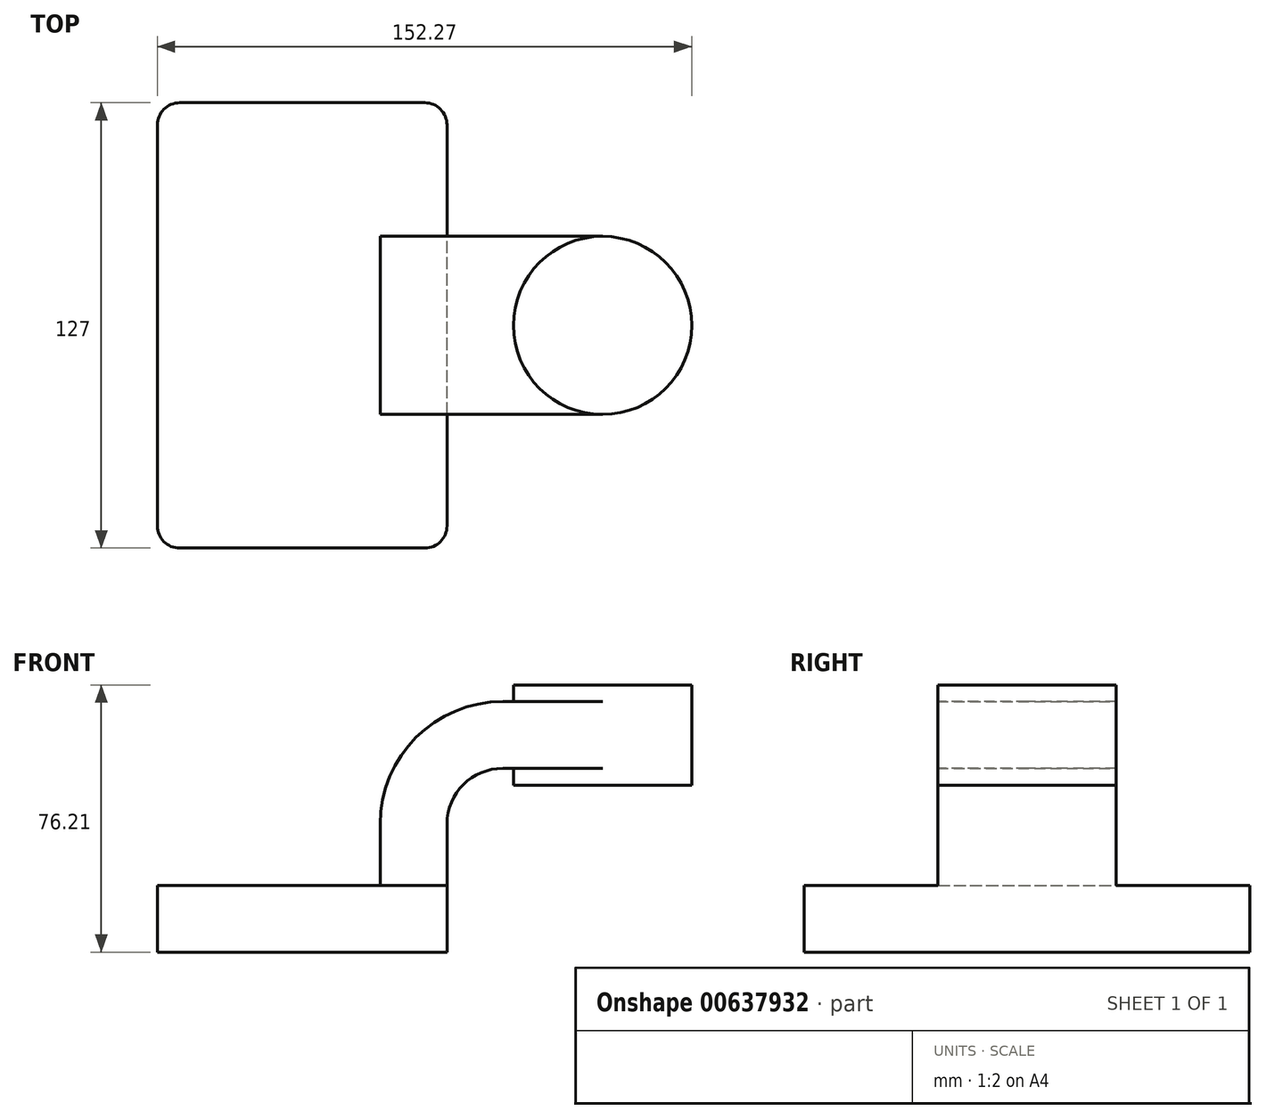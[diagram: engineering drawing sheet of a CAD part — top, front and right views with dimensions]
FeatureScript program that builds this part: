
annotation { "Feature Type Name" : "Feature", "Feature Type Description" : "" }
export const myFeature = defineFeature(function(context is Context, id is Id, definition is map)
    precondition{}
    {
        {
            var Q0;
            Q0=qCreatedBy(makeId("Front.planeOp"),FACE);
            var sketch = newSketch(context, id + "F0", { "sketchPlane" : qUnion([Q0])});
            skLineSegment(sketch, "E0.bottom", {"start": v(-41.28, -9.53) * mm, "end": v(41.28, -9.53) * mm});
            skLineSegment(sketch, "E0.top", {"start": v(-41.28, 9.53) * mm, "end": v(41.28, 9.53) * mm});
            skLineSegment(sketch, "E0.left", {"start": v(-41.28, -9.53) * mm, "end": v(-41.28, 9.53) * mm});
            skLineSegment(sketch, "E0.right", {"start": v(41.28, -9.53) * mm, "end": v(41.28, 9.53) * mm});
            skPoint(sketch, "E0.middle", {"position": v(0, 0) * mm});
            skLineSegment(sketch, "E1", {"start": v(41.28, 9.53) * mm, "end": v(41.28, 27) * mm});
            skArc(sketch, "E2", {"start": v(41.27, 27) * mm, "mid": v(45.92, 38.23) * mm, "end": v(57.15, 42.88) * mm});
            skLineSegment(sketch, "E3.bottom", {"start": v(60.2, 38.1) * mm, "end": v(111, 38.1) * mm});
            skLineSegment(sketch, "E3.top", {"start": v(60.2, 66.67) * mm, "end": v(111, 66.67) * mm});
            skLineSegment(sketch, "E3.left", {"start": v(60.2, 38.1) * mm, "end": v(60.2, 66.67) * mm});
            skLineSegment(sketch, "E3.right", {"start": v(111, 38.1) * mm, "end": v(111, 66.67) * mm});
            skPoint(sketch, "E3.middle", {"position": v(85.6, 52.39) * mm});
            skLineSegment(sketch, "E4", {"start": v(57.15, 42.88) * mm, "end": v(85.72, 42.88) * mm});
            skLineSegment(sketch, "E5.0", {"start": v(57.15, 61.93) * mm, "end": v(85.6, 61.93) * mm});
            skArc(sketch, "E5.1", {"start": v(22.23, 27) * mm, "mid": v(32.45, 51.7) * mm, "end": v(57.15, 61.93) * mm});
            skLineSegment(sketch, "E5.2", {"start": v(22.23, 9.53) * mm, "end": v(22.23, 27) * mm});
            skLineSegment(sketch, "E6", {"start": v(85.6, 38.1) * mm, "end": v(85.6, 66.67) * mm});
            skFitSpline(sketch, "E7", {"points": [v(-41.28, 9.53) * mm, v(57.15, 61.93) * mm], "startDerivative": vector(2.36, 68.58) * mm, "endDerivative": vector(171.45, -0.03) * mm});
            skSolve(sketch);
        }
        {
            var Q0;
            Q0=makeQuery(id+"F0.imprint","IMPRINT",FACE,{"disambiguationData":[TD([[makeQuery(id+"F0.imprint","IMPRINT",EDGE,{"derivedFrom":sQuery(id+"F0.wireOp",EDGE,"E0.bottom")}),1.0]])]});
            extrude(context, id + "F1", {"entities" : qUnion([Q0]), "endBound" : BoundingType.SYMMETRIC, "depth" : 127 * mm, "offsetDistance" : 25.4 * mm});
        }
        {
            var Q0;
            {var subQ5=sQuery(id+"F0.wireOp",EDGE,"E1");Q0=makeQuery(id+"F0.imprint","IMPRINT",FACE,{"disambiguationData":[TD([[makeQuery(id+"F0.imprint","IMPRINT",EDGE,{"derivedFrom":subQ5}),1.0]])]});}
            var Q1;
            {var subQ0=sQuery(id+"F0.wireOp",EDGE,"E4");var subQ1=sQuery(id+"F0.wireOp",EDGE,"E3.left");var subQ2=makeQuery(id+"F0.imprint","INTERSECT",VERTEX,{"derivedFrom":[subQ1,subQ0]});Q1=makeQuery(id+"F0.imprint","IMPRINT",FACE,{"disambiguationData":[TD([[makeQuery(id+"F0.imprint","IMPRINT",EDGE,{"disambiguationData":[TD([[subQ2,-1.0]])],"derivedFrom":subQ1}),-1.0]])]});}
            extrude(context, id + "F2", {"entities" : qUnion([Q0, Q1]), "operationType" : NewBodyOperationType.ADD, "endBound" : BoundingType.SYMMETRIC, "depth" : 50.8 * mm, "offsetDistance" : 25.4 * mm});
        }
        {
            var Q0;
            Q0=makeQuery(id+"F0.imprint","IMPRINT",FACE,{"disambiguationData":[TD([[makeQuery(id+"F0.imprint","IMPRINT",EDGE,{"derivedFrom":sQuery(id+"F0.wireOp",EDGE,"E5.1")}),1.0]])]});
            extrude(context, id + "F3", {"entities" : qUnion([Q0]), "operationType" : NewBodyOperationType.ADD, "endBound" : BoundingType.SYMMETRIC, "depth" : 15.88 * mm, "offsetDistance" : 25.4 * mm});
        }
        {
            var Q0;
            {var subQ4=sQuery(id+"F0.wireOp",EDGE,"E3.right");Q0=makeQuery(id+"F0.imprint","IMPRINT",FACE,{"disambiguationData":[TD([[makeQuery(id+"F0.imprint","IMPRINT",EDGE,{"derivedFrom":subQ4}),1.0]])]});}
            var Q1;
            Q1=sQuery(id+"F0.wireOp",EDGE,"E6");
            revolve(context, id + "F4", {"operationType" : NewBodyOperationType.ADD, "entities" : qUnion([Q0]), "axis" : qUnion([Q1]), "revolveType" : RevolveType.FULL});
        }
        {
            var Q0;
            Q0=makeQuery(id+"F1.opExtrude","CAP_EDGE",EDGE,{"disambiguationData":[OSD([sQuery(id+"F0.wireOp",EDGE,"E0.left")])],"isStart":false});
            var Q1;
            Q1=makeQuery(id+"F1.opExtrude","CAP_EDGE",EDGE,{"disambiguationData":[OSD([sQuery(id+"F0.wireOp",EDGE,"E0.right")])],"isStart":false});
            var Q2;
            Q2=makeQuery(id+"F1.opExtrude","CAP_EDGE",EDGE,{"disambiguationData":[OSD([sQuery(id+"F0.wireOp",EDGE,"E0.right")])],"isStart":true});
            var Q3;
            Q3=makeQuery(id+"F1.opExtrude","CAP_EDGE",EDGE,{"disambiguationData":[OSD([sQuery(id+"F0.wireOp",EDGE,"E0.left")])],"isStart":true});
            fillet(context, id + "F5", {"entities" : qUnion([Q0, Q1, Q2, Q3]), "radius" : 6.35 * mm, "tangentPropagation" : true, "allowEdgeOverflow" : false});
        }
    });
